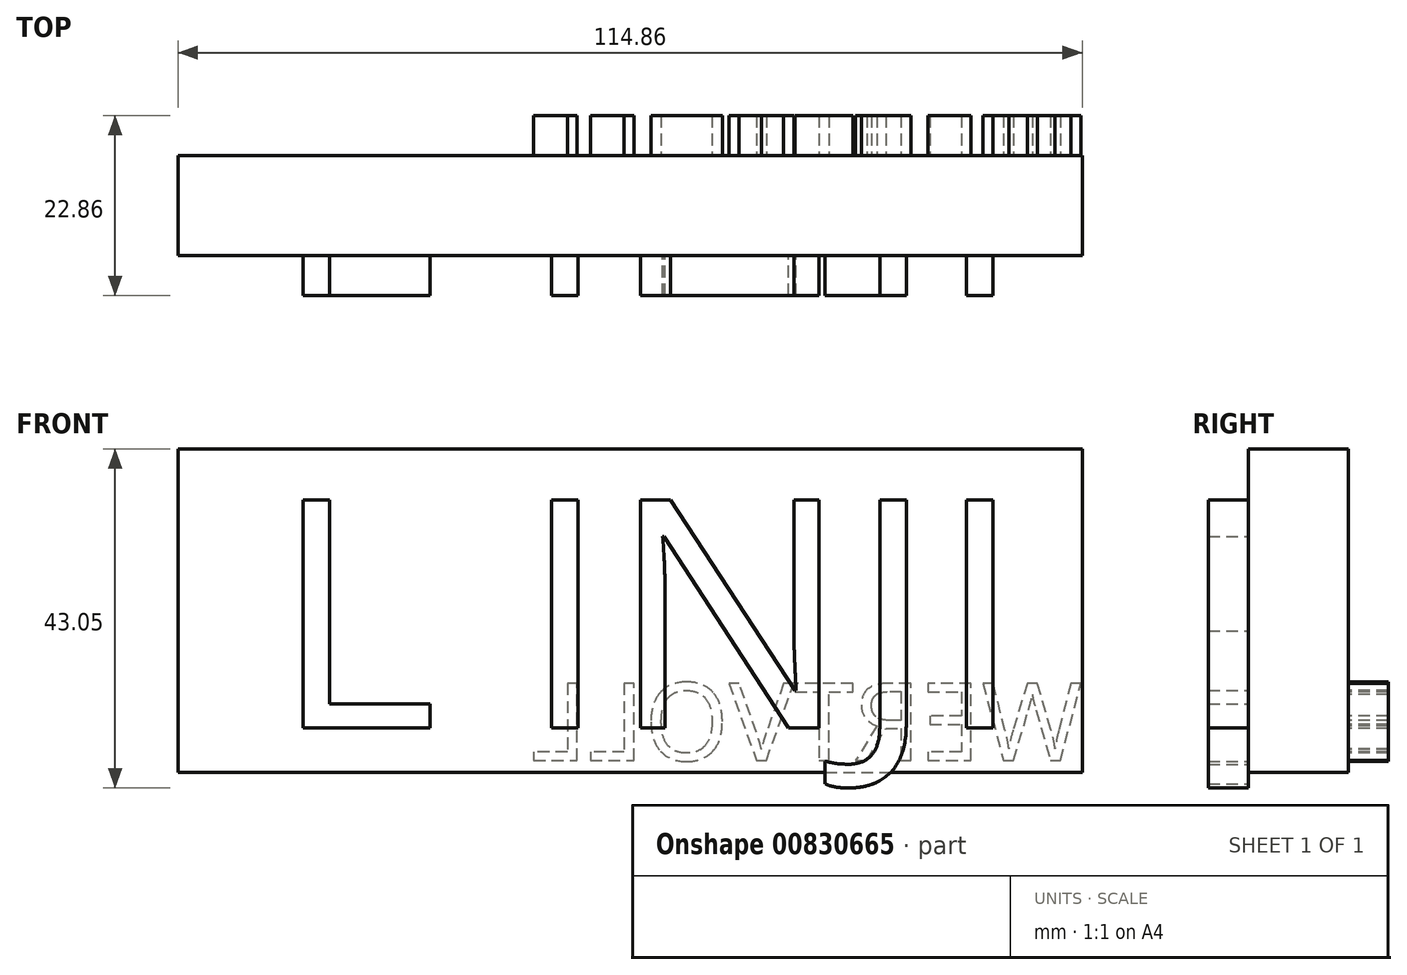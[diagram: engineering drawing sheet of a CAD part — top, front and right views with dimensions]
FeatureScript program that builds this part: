
annotation { "Feature Type Name" : "Feature", "Feature Type Description" : "" }
export const myFeature = defineFeature(function(context is Context, id is Id, definition is map)
    precondition{}
    {
        {
            var Q0;
            Q0=qCreatedBy(makeId("Front.planeOp"),FACE);
            var sketch = newSketch(context, id + "F0", { "sketchPlane" : qUnion([Q0])});
            skLineSegment(sketch, "E0.bottom", {"start": v(0, 0) * mm, "end": v(114.86, 0) * mm});
            skLineSegment(sketch, "E0.top", {"start": v(0, 41.08) * mm, "end": v(114.86, 41.08) * mm});
            skLineSegment(sketch, "E0.left", {"start": v(0, 0) * mm, "end": v(0, 41.08) * mm});
            skLineSegment(sketch, "E0.right", {"start": v(114.86, 0) * mm, "end": v(114.86, 41.08) * mm});
            skSolve(sketch);
        }
        {
            var Q0;
            Q0=makeQuery(id+"F0.imprint","IMPRINT",FACE,{"disambiguationData":[TD([[makeQuery(id+"F0.imprint","IMPRINT",EDGE,{"derivedFrom":sQuery(id+"F0.wireOp",EDGE,"E0.bottom")}),1.0]])]});
            extrude(context, id + "F1", {"entities" : qUnion([Q0]), "depth" : 12.7 * mm, "offsetDistance" : 25.4 * mm});
        }
        {
            var Q0;
            Q0=makeQuery(id+"F1.opExtrude","CAP_FACE",FACE,{"disambiguationData":[OSD([sQuery(id+"F0.wireOp",EDGE,"E0.bottom"),sQuery(id+"F0.wireOp",EDGE,"E0.top"),sQuery(id+"F0.wireOp",EDGE,"E0.left"),sQuery(id+"F0.wireOp",EDGE,"E0.right")])],"isStart":false});
            var sketch = newSketch(context, id + "F2", { "sketchPlane" : qUnion([Q0])});
            skText(sketch, "E1", { "text": "L INJI", "fontName": "OpenSans-Regular.ttf"});
            const initialGuessF2  = {"E1": [0.0119, 0.00565, 1, 0, 0.0292]};
            skSetInitialGuess(sketch, initialGuessF2);
            skSolve(sketch);
        }
        {
            var Q0;
            Q0 = qSketchRegion(id + "F2", true);
            extrude(context, id + "F3", {"entities" : qUnion([Q0]), "operationType" : NewBodyOperationType.ADD, "depth" : 5.08 * mm, "offsetDistance" : 25.4 * mm});
        }
        {
            var Q0;
            Q0=makeQuery(id+"F1.opExtrude","CAP_FACE",FACE,{"disambiguationData":[OSD([sQuery(id+"F0.wireOp",EDGE,"E0.bottom"),sQuery(id+"F0.wireOp",EDGE,"E0.top"),sQuery(id+"F0.wireOp",EDGE,"E0.left"),sQuery(id+"F0.wireOp",EDGE,"E0.right")])],"isStart":true});
            var sketch = newSketch(context, id + "F4", { "sketchPlane" : qUnion([Q0])});
            skText(sketch, "E2", { "text": "WERTVOLL", "fontName": "NotoSans-Regular.ttf"});
            const initialGuessF4  = {"E2": [-0.11486, 0.00152, 1, 0, 0.0099]};
            skSetInitialGuess(sketch, initialGuessF4);
            skSolve(sketch);
        }
        {
            var Q0;
            Q0 = qSketchRegion(id + "F4", true);
            extrude(context, id + "F5", {"entities" : qUnion([Q0]), "operationType" : NewBodyOperationType.ADD, "depth" : 5.08 * mm, "offsetDistance" : 25.4 * mm});
        }
    });
